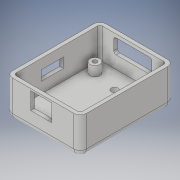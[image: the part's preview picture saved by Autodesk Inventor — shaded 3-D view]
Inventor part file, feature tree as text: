
AUTODESK INVENTOR PART (.ipt)
format: ipt  version: 2019.4 (Build 234330000, 330)  size: 246,784 bytes
history: native  units: mm
features: extrude x7, sketch x7, fillet x5, plane x1
ambient origin geometry x8: Origin, YZ Plane, XZ Plane, XY Plane, X Axis, Y Axis, Z Axis, Center Point
bodies: Solid1 (feature_tree)
feature tree (20):
  extrude  "Extrusion1"  Depth=76.0mm
  extrude  "Extrusion2"  Depth=3.0mm
  extrude  "Extrusion3"  Depth=54.0mm
  extrude  "Extrusion4"  Depth=25.0mm TaperAngle=0.0deg
  plane  "Work Plane1"
  fillet  "Fillet1"  Radius=15.0mm
  fillet  "Fillet2"  Radius=5.5mm
  fillet  "Fillet3"  Radius=5.5mm
  fillet  "Fillet4"  Radius=15.0mm
  extrude  "Extrusion8"  Depth=4.0mm
  fillet  "Fillet7"  Radius=7.0mm
  extrude  "Extrusion9"  Depth=3.5mm
  extrude  "Extrusion10"  Depth=8.0mm TaperAngle=0.0deg
  sketch  "Sketch1"  dims[d0=60.0mm d1=76.0mm]
  sketch  "Sketch2"  dims[d2=30.0mm d3=0.0mm d4=3.0mm]
  sketch  "Sketch3"  dims[d5=3.0mm d6=54.0mm]
  sketch  "Sketch4"  dims[d7=70.0mm d8=25.0mm d9=0.0mm d10=15.0mm d12=5.5mm d13=5.5mm d14=15.0mm d15=0.0mm]
  sketch  "Sketch8"  dims[d16=8.0mm d17=4.0mm d18=7.0mm]
  sketch  "Sketch9"  dims[d19=20.0mm d21=55.0mm d22=20.0mm d24=38.0mm d27=3.5mm]
  sketch  "Sketch10"  dims[d28=20.0mm d30=55.0mm d31=20.0mm d33=38.0mm d36=8.0mm d37=0.0mm d67=-50.0mm d78=5.0mm d79=5.0mm d80=2.0mm d81=2.0mm d85=27.0mm d86=15.0mm d87=14.75mm d88=2.73mm d89=31.0mm d90=12.0mm d91=10.0mm d92=0.0mm d93=2.0mm d94=32.5mm d95=8.0mm d96=18.0mm d97=8.0mm d98=3.0mm d99=0.0mm d100=19.88mm d101=1.5mm d102=17.0mm d103=14.0mm d104=3.0mm d105=0.0mm]
